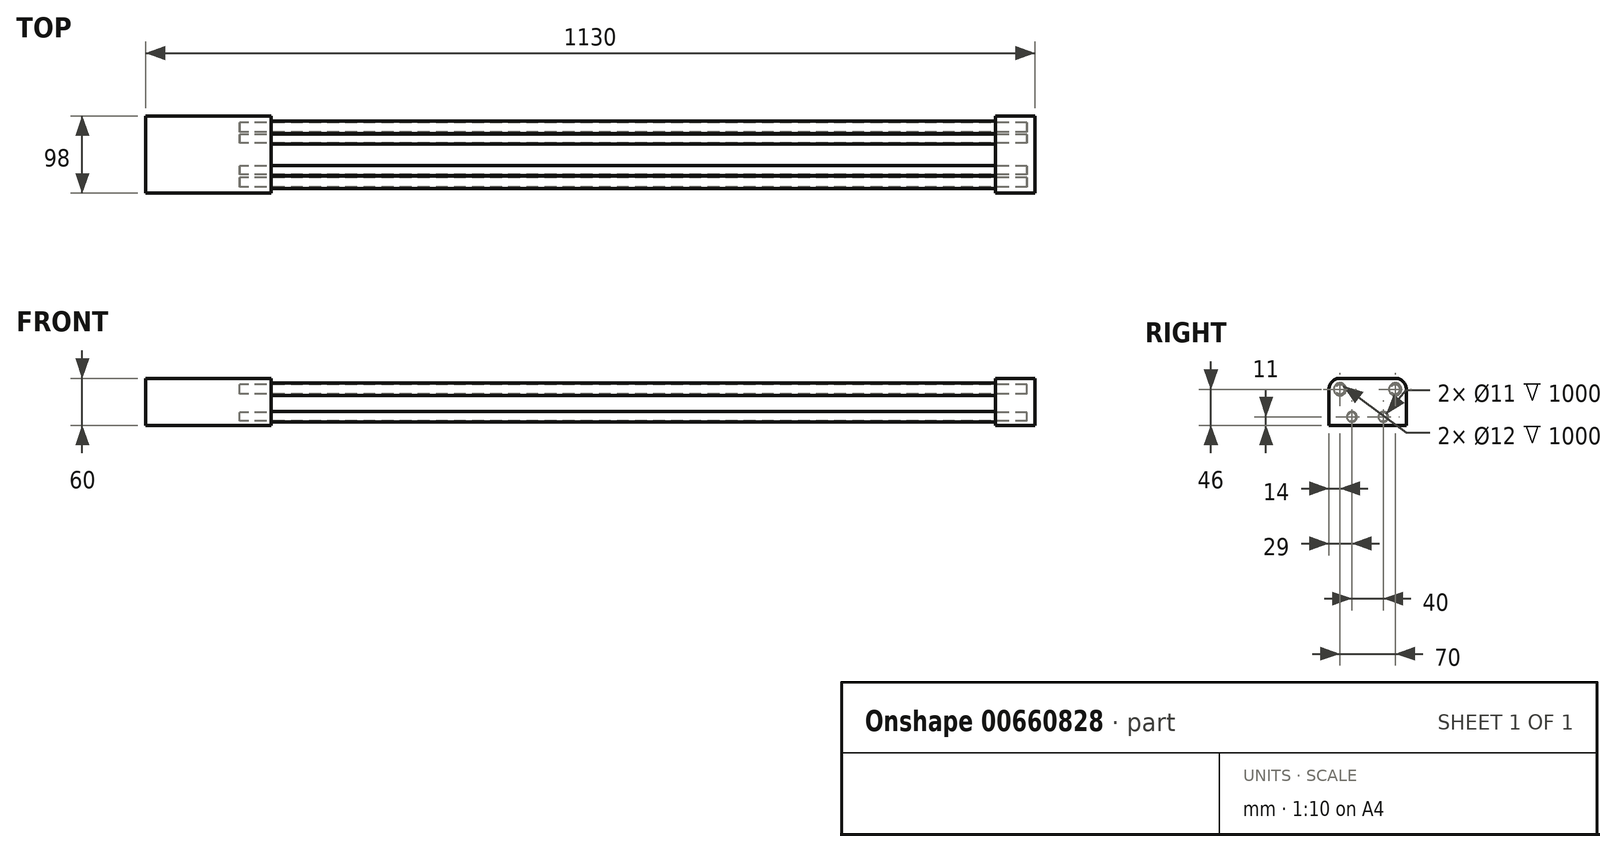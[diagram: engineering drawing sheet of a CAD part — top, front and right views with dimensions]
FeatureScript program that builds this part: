
annotation { "Feature Type Name" : "Feature", "Feature Type Description" : "" }
export const myFeature = defineFeature(function(context is Context, id is Id, definition is map)
    precondition{}
    {
        {
            var Q0;
            Q0=qCreatedBy(makeId("Right.planeOp"),FACE);
            var sketch = newSketch(context, id + "F0", { "sketchPlane" : qUnion([Q0])});
            skCircle(sketch, "E0", {"center": v(35, 0) * mm, "radius": 8 * mm});
            skCircle(sketch, "E1", {"center": v(-35, 0) * mm, "radius": 8 * mm});
            skCircle(sketch, "E2", {"center": v(-35, 0) * mm, "radius": 6 * mm});
            skCircle(sketch, "E3", {"center": v(35, 0) * mm, "radius": 6 * mm});
            skCircle(sketch, "E4", {"center": v(-20, -35) * mm, "radius": 6.5 * mm});
            skCircle(sketch, "E5", {"center": v(20, -35) * mm, "radius": 6.5 * mm});
            skCircle(sketch, "E6", {"center": v(-20, -35) * mm, "radius": 5.5 * mm});
            skCircle(sketch, "E7", {"center": v(20, -35) * mm, "radius": 5.5 * mm});
            skSolve(sketch);
        }
        {
            var Q0;
            Q0 = qSketchRegion(id + "F0", true);
            extrude(context, id + "F1", {"entities" : qUnion([Q0]), "depth" : 500 * mm, "offsetDistance" : 25 * mm, "hasSecondDirection" : true, "secondDirectionOppositeDirection" : true, "secondDirectionDepth" : 500 * mm});
        }
        {
            var Q0;
            Q0=makeQuery(id+"F1.opExtrude","CAP_FACE",FACE,{"disambiguationData":[OSD([sQuery(id+"F0.wireOp",EDGE,"E0"),sQuery(id+"F0.wireOp",EDGE,"E3")])],"isStart":false});
            var sketch = newSketch(context, id + "F2", { "sketchPlane" : qUnion([Q0])});
            skLineSegment(sketch, "E8.bottom", {"start": v(-49, 14) * mm, "end": v(49, 14) * mm});
            skLineSegment(sketch, "E8.top", {"start": v(-49, -46) * mm, "end": v(49, -46) * mm});
            skLineSegment(sketch, "E8.left", {"start": v(-49, 14) * mm, "end": v(-49, -46) * mm});
            skLineSegment(sketch, "E8.right", {"start": v(49, 14) * mm, "end": v(49, -46) * mm});
            skPoint(sketch, "E8.middle", {"position": v(0, -16) * mm});
            skCircle(sketch, "E9.0", {"center": v(-35, 0) * mm, "radius": 8 * mm});
            skCircle(sketch, "E10.0", {"center": v(-20, -35) * mm, "radius": 6.5 * mm});
            skCircle(sketch, "E11.0", {"center": v(20, -35) * mm, "radius": 6.5 * mm});
            skCircle(sketch, "E12.0", {"center": v(35, 0) * mm, "radius": 8 * mm});
            skSolve(sketch);
        }
        {
            var Q0;
            Q0=makeQuery(id+"F2.imprint","IMPRINT",FACE,{"disambiguationData":[TD([[makeQuery(id+"F2.imprint","IMPRINT",EDGE,{"derivedFrom":sQuery(id+"F2.wireOp",EDGE,"E8.bottom")}),-1.0]])]});
            extrude(context, id + "F3", {"entities" : qUnion([Q0]), "oppositeDirection" : true, "depth" : 40 * mm, "offsetDistance" : 25 * mm});
        }
        {
            var Q0;
            Q0=makeQuery(id+"F3.opExtrude","CAP_FACE",FACE,{"disambiguationData":[OSD([sQuery(id+"F2.wireOp",EDGE,"E8.bottom"),sQuery(id+"F2.wireOp",EDGE,"E8.top"),sQuery(id+"F2.wireOp",EDGE,"E8.left"),sQuery(id+"F2.wireOp",EDGE,"E8.right"),sQuery(id+"F2.wireOp",EDGE,"E9.0"),sQuery(id+"F2.wireOp",EDGE,"E10.0"),sQuery(id+"F2.wireOp",EDGE,"E11.0"),sQuery(id+"F2.wireOp",EDGE,"E12.0")])],"isStart":true});
            var sketch = newSketch(context, id + "F4", { "sketchPlane" : qUnion([Q0])});
            skLineSegment(sketch, "E13.0.0", {"start": v(-49, 14) * mm, "end": v(-49, -46) * mm});
            skLineSegment(sketch, "E13.0.1", {"start": v(-49, -46) * mm, "end": v(49, -46) * mm});
            skLineSegment(sketch, "E13.0.2", {"start": v(49, -46) * mm, "end": v(49, 14) * mm});
            skLineSegment(sketch, "E13.0.3", {"start": v(49, 14) * mm, "end": v(-49, 14) * mm});
            skSolve(sketch);
        }
        {
            var Q0;
            Q0 = qSketchRegion(id + "F4", true);
            extrude(context, id + "F5", {"entities" : qUnion([Q0]), "operationType" : NewBodyOperationType.ADD, "depth" : 10 * mm, "offsetDistance" : 25 * mm});
        }
        {
            var Q0;
            Q0=makeQuery(id+"F5.boolean.opBoolean","MERGE",EDGE,{"derivedFrom":[makeQuery(id+"F3.opExtrude","SWEPT_EDGE",EDGE,{"disambiguationData":[OSD([sQuery(id+"F2.wireOp",EDGE,"E8.bottom"),sQuery(id+"F2.wireOp",EDGE,"E8.left")])]}),makeQuery(id+"F5.opExtrude","SWEPT_EDGE",EDGE,{"disambiguationData":[OSD([sQuery(id+"F4.wireOp",EDGE,"E13.0.0"),sQuery(id+"F4.wireOp",EDGE,"E13.0.3")])]})]});
            var Q1;
            Q1=makeQuery(id+"F5.boolean.opBoolean","MERGE",EDGE,{"derivedFrom":[makeQuery(id+"F3.opExtrude","SWEPT_EDGE",EDGE,{"disambiguationData":[OSD([sQuery(id+"F2.wireOp",EDGE,"E8.bottom"),sQuery(id+"F2.wireOp",EDGE,"E8.right")])]}),makeQuery(id+"F5.opExtrude","SWEPT_EDGE",EDGE,{"disambiguationData":[OSD([sQuery(id+"F4.wireOp",EDGE,"E13.0.2"),sQuery(id+"F4.wireOp",EDGE,"E13.0.3")])]})]});
            fillet(context, id + "F6", {"entities" : qUnion([Q0, Q1]), "radius" : 14 * mm, "tangentPropagation" : true, "allowEdgeOverflow" : false});
        }
        {
            var Q0;
            Q0=makeQuery(id+"F1.opExtrude","CAP_FACE",FACE,{"disambiguationData":[OSD([sQuery(id+"F0.wireOp",EDGE,"E0"),sQuery(id+"F0.wireOp",EDGE,"E3")])],"isStart":true});
            var sketch = newSketch(context, id + "F7", { "sketchPlane" : qUnion([Q0])});
            skLineSegment(sketch, "E14.0.0", {"start": v(35, 14) * mm, "end": v(-35, 14) * mm});
            skArc(sketch, "E14.0.1", {"start": v(-35, 14) * mm, "mid": v(-44.9, 9.9) * mm, "end": v(-49, 0) * mm});
            skLineSegment(sketch, "E14.0.2", {"start": v(-49, 0) * mm, "end": v(-49, -46) * mm});
            skLineSegment(sketch, "E14.0.3", {"start": v(-49, -46) * mm, "end": v(49, -46) * mm});
            skLineSegment(sketch, "E14.0.4", {"start": v(49, -46) * mm, "end": v(49, 0) * mm});
            skArc(sketch, "E14.0.5", {"start": v(49, 0) * mm, "mid": v(44.9, 9.9) * mm, "end": v(35, 14) * mm});
            skCircle(sketch, "E15.0", {"center": v(-35, 0) * mm, "radius": 8 * mm});
            skCircle(sketch, "E16.0", {"center": v(35, 0) * mm, "radius": 8 * mm});
            skCircle(sketch, "E17.0", {"center": v(20, -35) * mm, "radius": 6.5 * mm});
            skCircle(sketch, "E18.0", {"center": v(-20, -35) * mm, "radius": 6.5 * mm});
            skSolve(sketch);
        }
        {
            var Q0;
            Q0 = qSketchRegion(id + "F7", true);
            extrude(context, id + "F8", {"entities" : qUnion([Q0]), "oppositeDirection" : true, "depth" : 40 * mm, "offsetDistance" : 25 * mm});
        }
        {
            var Q0;
            Q0=makeQuery(id+"F8.opExtrude","CAP_FACE",FACE,{"disambiguationData":[OSD([sQuery(id+"F7.wireOp",EDGE,"E14.0.0"),sQuery(id+"F7.wireOp",EDGE,"E14.0.1"),sQuery(id+"F7.wireOp",EDGE,"E14.0.2"),sQuery(id+"F7.wireOp",EDGE,"E14.0.3"),sQuery(id+"F7.wireOp",EDGE,"E14.0.4"),sQuery(id+"F7.wireOp",EDGE,"E14.0.5"),sQuery(id+"F7.wireOp",EDGE,"E15.0"),sQuery(id+"F7.wireOp",EDGE,"E16.0"),sQuery(id+"F7.wireOp",EDGE,"E17.0"),sQuery(id+"F7.wireOp",EDGE,"E18.0")])],"isStart":true});
            var sketch = newSketch(context, id + "F9", { "sketchPlane" : qUnion([Q0])});
            skLineSegment(sketch, "E19.0.0", {"start": v(49, -46) * mm, "end": v(49, 0) * mm});
            skArc(sketch, "E19.0.1", {"start": v(49, 0) * mm, "mid": v(44.9, 9.9) * mm, "end": v(35, 14) * mm});
            skLineSegment(sketch, "E19.0.2", {"start": v(35, 14) * mm, "end": v(-35, 14) * mm});
            skArc(sketch, "E19.0.3", {"start": v(-35, 14) * mm, "mid": v(-44.9, 9.9) * mm, "end": v(-49, 0) * mm});
            skLineSegment(sketch, "E19.0.4", {"start": v(-49, 0) * mm, "end": v(-49, -46) * mm});
            skLineSegment(sketch, "E19.0.5", {"start": v(-49, -46) * mm, "end": v(49, -46) * mm});
            skSolve(sketch);
        }
        {
            var Q0;
            Q0 = qSketchRegion(id + "F9", true);
            extrude(context, id + "F10", {"entities" : qUnion([Q0]), "operationType" : NewBodyOperationType.ADD, "depth" : 120 * mm, "offsetDistance" : 25 * mm});
        }
    });
